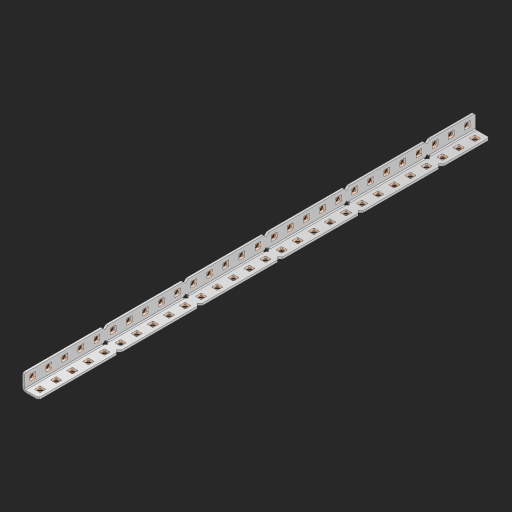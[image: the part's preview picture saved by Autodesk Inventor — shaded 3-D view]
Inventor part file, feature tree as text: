
AUTODESK INVENTOR PART (.ipt)
format: ipt  version: 2023 (Build 270158000, 158)  size: 984,576 bytes
history: native  units: in
note: dims shown in document units (in); Inventor stores cm internally (conversion verified against a paired STEP export)
features: other x62, extrude x57, sheet_metal_op x8, sketch x5, pattern_linear x1, mirror x1, chamfer x1
ambient origin geometry x8: Origin, YZ Plane, XZ Plane, XY Plane, X Axis, Y Axis, Z Axis, Center Point
bodies: Solid1 (feature_tree), Body (feature_tree)
feature tree (135):
  sheet_metal_op  "Flanges"
  sheet_metal_op  "Body Pattern"
  other  "Arc Length"
  pattern_linear  "Notch Pattern"  Spacing1=0.125in  [1 undecoded]
  other  "Diagonal Plane"
  mirror  "Everything Mirrored"
  chamfer  "End Chamfer"
  sketch  "Sketch1"  dims[d0=0.5in]
  other  "Plate1"
  sketch  "Sketch2"  dims[d1=14.0in]
  other  "Plate2"
  sheet_metal_op  "Bend1"
  sheet_metal_op  "Corner1"
  sketch  "Sketch8"  dims[d2=0.0625in]
  sketch  "Sketch9"  dims[d3=0.0625in]
  other  "Srf91"
  sheet_metal_op  "Body Pattern Sketch"
  other  "Srf92"
  sketch  "Sketch13"  dims[d4=0.0312in d5=0.125in d6=0.0625in d7=0.5in d8=90.0deg d9=0.0312in d10=0.25in d11=0.0625in d12=0.0625in d49=0.182in d50=0.02in d52=0.25in d53=0.0625in d54=0.0in d55=0.172in d56=1.0in d57=0.0in d85=0.1473in d86=0.1782in d89=0.0625in d90=0.0in d91=0.04in d92=0.0491in d95=2.5in d96=0.04in d97=0.25in d98=45.0deg d123=0.204in d126=0.0491in d127=0.1473in d128=0.08in d129=0.04in d130=2.5in d131=11.0236in d133=0.5in d134=0.3937in d136=1.0in]
  other  "Srf856"
  other  "Srf857"
  other  "Srf858"
  other  "Srf859"
  other  "Srf860"
  other  "Srf861"
  other  "Srf1275"
  other  "Srf1276"
  other  "Srf1278"
  other  "Srf1279"
  other  "Srf1280"
  other  "Srf1281"
  other  "Srf1282"
  other  "Srf1283"
  other  "Srf1383"
  other  "Srf1384"
  other  "Srf1385"
  other  "Srf1386"
  other  "Srf1387"
  other  "Srf1388"
  other  "Srf1389"
  other  "Srf1390"
  other  "Srf1391"
  other  "Srf1392"
  other  "Srf1393"
  other  "Srf1394"
  other  "Srf1395"
  other  "Srf1396"
  other  "Srf1397"
  other  "Srf1398"
  other  "Srf1399"
  other  "Srf1400"
  other  "Srf1401"
  other  "Srf1402"
  other  "Srf1403"
  other  "Srf1475"
  other  "Srf1476"
  other  "Srf1477"
  other  "Srf1478"
  other  "Srf1479"
  other  "Srf1480"
  other  "Srf1481"
  other  "Srf1482"
  other  "Srf1483"
  other  "Srf1484"
  other  "Srf1485"
  other  "Srf1486"
  other  "Srf1487"
  other  "Srf1488"
  other  "Srf1489"
  other  "Srf1490"
  other  "Srf1491"
  other  "Srf1492"
  other  "Srf1493"
  other  "Srf1494"
  other  "Srf1495"
  sheet_metal_op  "Body Stamp"
  sheet_metal_op  "Body Circle"
  sheet_metal_op  "Notch"
  extrude  "ExtrusionSrf92"  Depth=0.0625in
  extrude  "ExtrusionSrf856"  Depth=0.5in TaperAngle=90.0deg
  extrude  "ExtrusionSrf857"  Depth=0.25in
  extrude  "ExtrusionSrf858"  Depth=0.0625in
  extrude  "ExtrusionSrf859"  Depth=0.0625in
  extrude  "ExtrusionSrf860"  Depth=0.3937in
  extrude  "ExtrusionSrf861"  Depth=0.02in
  extrude  "ExtrusionSrf1275"  Depth=0.25in
  extrude  "ExtrusionSrf1276"  Depth=0.0625in
  extrude  "ExtrusionSrf1277"  TaperAngle=0.0deg  [1 undecoded]
  extrude  "ExtrusionSrf1278"  Depth=0.3937in
  extrude  "ExtrusionSrf1279"  Depth=0.3937in TaperAngle=0.0deg
  extrude  "ExtrusionSrf1280"  Depth=0.3937in
  extrude  "ExtrusionSrf1281"  Depth=0.3937in
  extrude  "ExtrusionSrf1282"  Depth=0.0625in
  extrude  "ExtrusionSrf1383"  Depth=0.3937in TaperAngle=0.0deg
  extrude  "ExtrusionSrf1384"  Depth=0.3937in
  extrude  "ExtrusionSrf1385"  Depth=0.25in TaperAngle=45.0deg
  extrude  "ExtrusionSrf1386"  Depth=0.3937in
  extrude  "ExtrusionSrf1387"  Depth=0.3937in
  extrude  "ExtrusionSrf1388"  Depth=0.3937in
  extrude  "ExtrusionSrf1389"  Depth=0.3937in
  extrude  "ExtrusionSrf1390"  Depth=0.3937in
  extrude  "ExtrusionSrf1391"  Depth=0.3937in
  extrude  "ExtrusionSrf1392"  Depth=0.3937in
  extrude  "ExtrusionSrf1393"  Depth=0.5in
  extrude  "ExtrusionSrf1394"  [1 undecoded]
  extrude  "ExtrusionSrf1395"  [1 undecoded]
  extrude  "ExtrusionSrf1396"  [1 undecoded]
  extrude  "ExtrusionSrf1397"  [1 undecoded]
  extrude  "ExtrusionSrf1398"  [1 undecoded]
  extrude  "ExtrusionSrf1399"  [1 undecoded]
  extrude  "ExtrusionSrf1400"  [1 undecoded]
  extrude  "ExtrusionSrf1401"  [1 undecoded]
  extrude  "ExtrusionSrf1402"  [1 undecoded]
  extrude  "ExtrusionSrf1403"  [1 undecoded]
  extrude  "ExtrusionSrf1475"  [1 undecoded]
  extrude  "ExtrusionSrf1476"  [1 undecoded]
  extrude  "ExtrusionSrf1477"  [1 undecoded]
  extrude  "ExtrusionSrf1478"  [1 undecoded]
  extrude  "ExtrusionSrf1479"  [1 undecoded]
  extrude  "ExtrusionSrf1480"  [1 undecoded]
  extrude  "ExtrusionSrf1481"  [1 undecoded]
  extrude  "ExtrusionSrf1482"  [1 undecoded]
  extrude  "ExtrusionSrf1483"  [1 undecoded]
  extrude  "ExtrusionSrf1484"  [1 undecoded]
  extrude  "ExtrusionSrf1485"  [1 undecoded]
  extrude  "ExtrusionSrf1486"  [1 undecoded]
  extrude  "ExtrusionSrf1487"  [1 undecoded]
  extrude  "ExtrusionSrf1488"  [1 undecoded]
  extrude  "ExtrusionSrf1489"  [1 undecoded]
  extrude  "ExtrusionSrf1490"  [1 undecoded]
  extrude  "ExtrusionSrf1491"  [1 undecoded]
  extrude  "ExtrusionSrf1492"  [1 undecoded]
  extrude  "ExtrusionSrf1493"  [1 undecoded]
  extrude  "ExtrusionSrf1494"  [1 undecoded]
  extrude  "ExtrusionSrf1495"  [1 undecoded]
note: 33 required parameter values undecoded (feature->parameter linkage not recoverable at this tier; creation-order binding heuristic only, values carry confidence <= 0.55)
